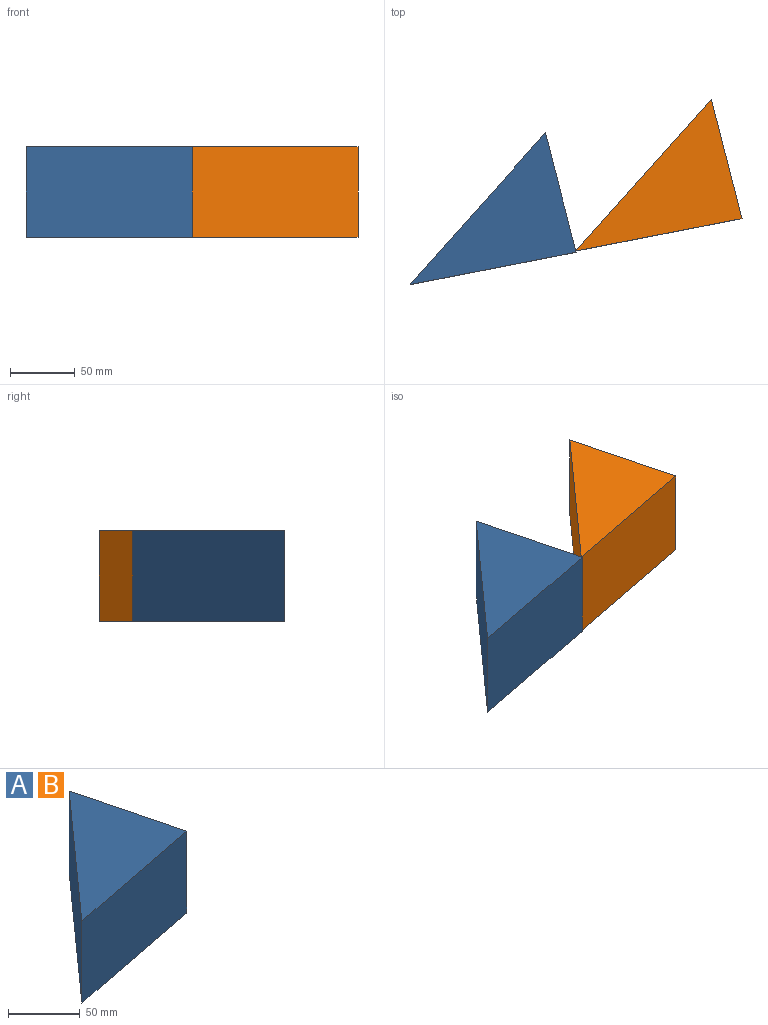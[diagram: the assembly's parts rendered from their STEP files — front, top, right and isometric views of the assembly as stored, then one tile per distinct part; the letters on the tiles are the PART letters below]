
ASSEMBLY  parts=2 mates=1
PART A: 5 faces, bbox 128.4x117.2x69.9 mm
  f0: plane 92.19x69.85mm, normal (0.97,0.25,0), area 6648.6mm2, adj f1,f2,f3,f4
  f1: plane 117.21x104.7mm, normal (-0.75,0.67,0), area 10977.5mm2, adj f0,f2,f3,f4
  f2: plane 128.4x69.85mm, normal (0.19,-0.98,0), area 9137.5mm2, adj f0,f1,f3,f4
  f3: plane 128.4x117.21mm, normal (0,0,1), area 6214.9mm2, adj f0,f1,f2
  f4: plane 128.4x117.21mm, normal (0,0,-1), area 6214.9mm2, adj f0,f1,f2
PART B: same geometry as A
PLACE A t=(-1.72,18.05,-1.55)mm fixed
PLACE B t=(126.51,43.94,-1.55)mm
MATE slider B.f2 <-> A.f2  axis (0.19,-0.98,0) through (65.52,-9.54,33.38)mm
